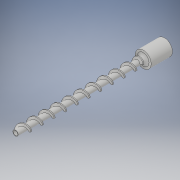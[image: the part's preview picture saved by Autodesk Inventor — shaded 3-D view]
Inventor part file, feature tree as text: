
AUTODESK INVENTOR PART (.ipt)
format: ipt  version: 2019 (Build 230136000, 136)  size: 362,496 bytes
history: native  units: mm
features: sketch x5, extrude x4, helix x1, fillet x1
ambient origin geometry x8: Origin, YZ Plane, XZ Plane, XY Plane, X Axis, Y Axis, Z Axis, Center Point
bodies: Solid1 (feature_tree)
feature tree (11):
  extrude  "Extrusion1"  Depth=20.0mm TaperAngle=0.0deg
  extrude  "Extrusion2"  Depth=5.5mm
  extrude  "Extrusion3"  Depth=5.0mm
  helix  "Coil1"  [1 undecoded]
  extrude  "Extrusion4"  Depth=2.5mm
  fillet  "Fillet2"  Radius=1.0mm
  sketch  "Sketch1"  dims[d0=15.0mm d1=20.0mm d2=0.0mm]
  sketch  "Sketch2"  dims[d3=5.5mm d4=4.8mm]
  sketch  "Sketch3"  dims[d5=15.0mm d6=0.0mm d7=5.0mm d8=120.0mm d9=0.0mm]
  sketch  "Sketch4"  dims[d10=2.0mm d11=2.5mm d12=1.0mm]
  sketch  "Sketch5"  dims[d13=3.0mm d14=11.0mm d15=10.0mm d16=102.0mm d17=0.0mm d18=90.0deg d19=90.0deg d20=0.0mm d21=0.0mm d23=4.2mm d24=125.0mm d25=0.0mm d26=3.0mm]
note: 1 required parameter value undecoded (feature->parameter linkage not recoverable at this tier; creation-order binding heuristic only, values carry confidence <= 0.55)
